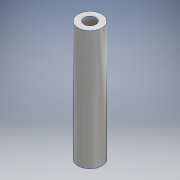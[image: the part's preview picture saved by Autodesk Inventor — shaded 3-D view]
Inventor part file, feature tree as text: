
AUTODESK INVENTOR PART (.ipt)
format: ipt  version: 2016 (Build 200138000, 138)  size: 104,960 bytes
history: native  units: mm
features: sketch x2, extrude x2, hole x2, other x1
ambient origin geometry x8: Origin, YZ Plane, XZ Plane, XY Plane, X Axis, Y Axis, Z Axis, Center Point
bodies: Body1 (feature_tree)
feature tree (7):
  other  "ソリッド1"
  sketch  "スケッチ1"
  extrude  "押し出し1"  Depth=6.0mm
  sketch  "スケッチ2"
  extrude  "押し出し2"  Depth=3.001mm
  hole  "穴1"  [1 undecoded]
  hole  "穴2"  [1 undecoded]
note: 2 required parameter values undecoded (feature->parameter linkage not recoverable at this tier; creation-order binding heuristic only, values carry confidence <= 0.55)
